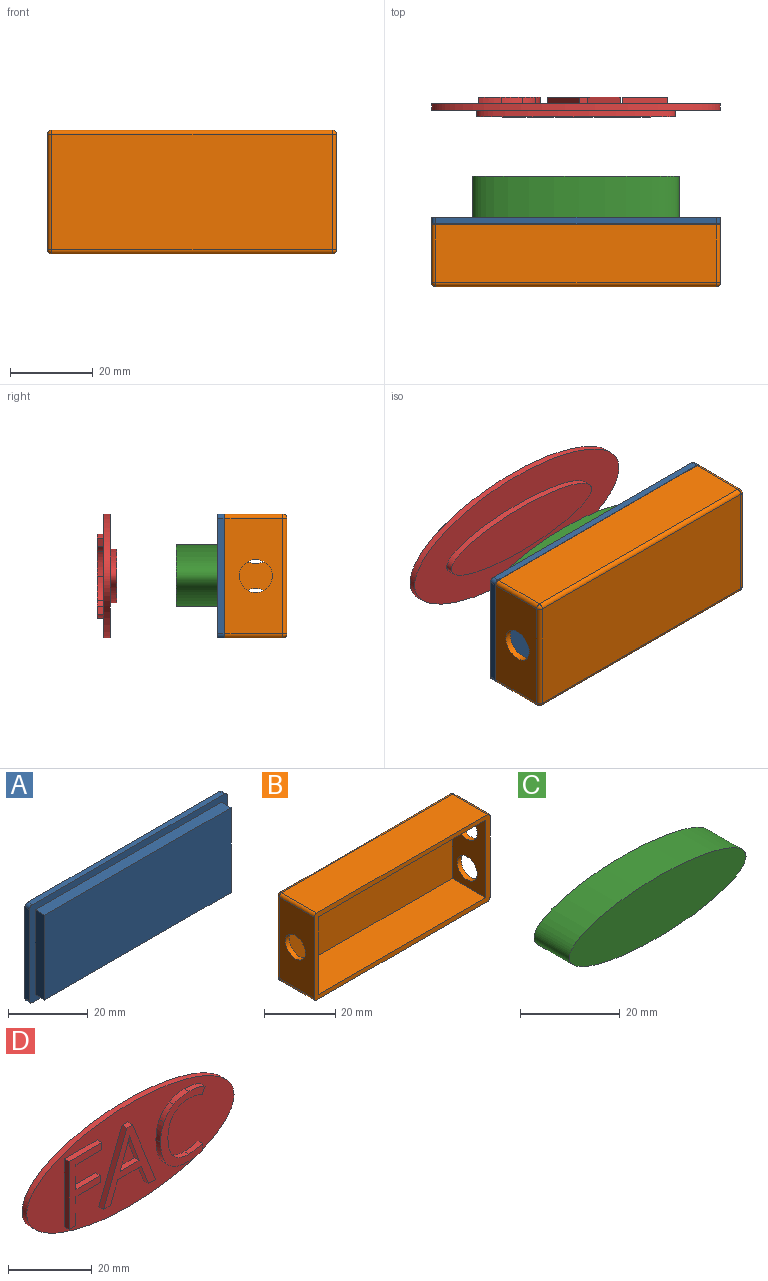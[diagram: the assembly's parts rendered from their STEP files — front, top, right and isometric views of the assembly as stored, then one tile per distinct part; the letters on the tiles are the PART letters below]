
ASSEMBLY  parts=4 mates=2
PART A: 15 faces, bbox 70x5x30 mm
  f0: plane 66x3.4mm, normal (0,0,1), area 224.4mm2, adj f1,f3,f4,f10
  f1: plane 26x3.4mm, normal (-1,0,0), area 88.4mm2, adj f0,f2,f4,f10
  f2: plane 66x3.4mm, normal (0,0,-1), area 224.4mm2, adj f1,f3,f4,f10
  f3: plane 26x3.4mm, normal (1,0,0), area 88.4mm2, adj f0,f2,f4,f10
  f4: plane 66x26mm, normal (0,-1,0), area 1716mm2, adj f0,f1,f2,f3
  f5: plane 70x30mm, normal (0,1,0), area 2099.1mm2, adj f6,f7,f8,f9,f11,f12,f13,f14
  f6: plane 68x1.6mm, normal (0,0,-1), area 108.8mm2, adj f5,f10,f11,f14
  f7: plane 28x1.6mm, normal (1,0,0), area 44.8mm2, adj f5,f10,f13,f14
  f8: plane 68x1.6mm, normal (0,0,1), area 108.8mm2, adj f5,f10,f12,f13
  f9: plane 28x1.6mm, normal (-1,0,0), area 44.8mm2, adj f5,f10,f11,f12
  f10: plane 70x30mm, normal (0,-1,0), area 383.1mm2, adj f0,f1,f2,f3,f6,f7,f8,f9
  f11: cylinder r=1mm len=1.6mm, axis (0,1,0), area 2.5mm2, adj f5,f6,f9,f10
  f12: cylinder r=1mm len=1.6mm, axis (0,-1,0), area 2.5mm2, adj f5,f8,f9,f10
  f13: cylinder r=1mm len=1.6mm, axis (0,1,0), area 2.5mm2, adj f5,f7,f8,f10
  f14: cylinder r=1mm len=1.6mm, axis (0,-1,0), area 2.5mm2, adj f5,f6,f7,f10
PART B: 26 faces, bbox 70x15x30 mm
  f0: plane 68x14mm, normal (0,0,1), area 952mm2, adj f8,f19,f23,f25
  f1: plane 28x14mm, normal (-1,0,0), area 341.7mm2, adj f8,f13,f16,f22,f25
  f2: plane 68x14mm, normal (0,0,-1), area 952mm2, adj f8,f14,f16,f17
  f3: plane 26.8x13.4mm, normal (-1,0,0), area 258.6mm2, adj f4,f6,f8,f10,f11,f12
  f4: plane 66.8x13.4mm, normal (0,0,1), area 895.1mm2, adj f3,f5,f8,f10
  f5: plane 26.8x13.4mm, normal (1,0,0), area 308.9mm2, adj f4,f6,f8,f10,f13
  f6: plane 66.8x13.4mm, normal (0,0,-1), area 895.1mm2, adj f3,f5,f8,f10
  f7: plane 28x14mm, normal (1,0,0), area 291.5mm2, adj f8,f11,f12,f14,f18,f19
  f8: plane 70x30mm, normal (0,-1,0), area 308.9mm2, adj f0,f1,f2,f3,f4,f5,f6,f7
  f9: plane 68x28mm, normal (0,1,0), area 1904mm2, adj f17,f18,f22,f23
  f10: plane 66.8x26.8mm, normal (0,-1,0), area 1790.2mm2, adj f3,f4,f5,f6
  f11: cylinder r=4mm len=8mm, axis (1,0,0), area 40.2mm2, adj f3,f7
  f12: cylinder r=4mm len=8mm, axis (1,0,0), area 40.2mm2, adj f3,f7
  f13: cylinder r=4mm len=8mm, axis (-1,0,0), area 40.2mm2, adj f1,f5
  f14: cylinder r=1mm len=14mm, axis (0,-1,0), area 22mm2, adj f2,f7,f8,f15
  f15: sphere r=1mm, area 1.6mm2, adj f14,f17,f18
  f16: cylinder r=1mm len=14mm, axis (0,1,0), area 22mm2, adj f1,f2,f8,f20
  f17: cylinder r=1mm len=68mm, axis (1,0,0), area 106.8mm2, adj f2,f9,f15,f20
  f18: cylinder r=1mm len=28mm, axis (0,0,1), area 44mm2, adj f7,f9,f15,f21
  f19: cylinder r=1mm len=14mm, axis (0,1,0), area 22mm2, adj f0,f7,f8,f21
  f20: sphere r=1mm, area 1.6mm2, adj f16,f17,f22
  f21: sphere r=1mm, area 1.6mm2, adj f18,f19,f23
  f22: cylinder r=1mm len=28mm, axis (0,0,-1), area 44mm2, adj f1,f9,f20,f24
  f23: cylinder r=1mm len=68mm, axis (-1,0,0), area 106.8mm2, adj f0,f9,f21,f24
  f24: sphere r=1mm, area 1.6mm2, adj f22,f23,f25
  f25: cylinder r=1mm len=14mm, axis (0,-1,0), area 22mm2, adj f0,f1,f8,f24
PART C: 5 faces, bbox 50x10x15 mm
  f0: extruded ~50x15mm, area 1097mm2, adj f1,f2
  f1: plane 50x15mm, normal (0,1,0), area 79.7mm2, adj f0,f3
  f2: plane 50x15mm, normal (0,-1,0), area 589mm2, adj f0
  f3: extruded ~48.4x13.4mm, area 168.1mm2, adj f1,f4
  f4: plane 48.4x13.4mm, normal (0,1,0), area 509.4mm2, adj f3
PART D: 47 faces, bbox 70x4.8x30 mm
  f0: extruded ~70x30mm, area 261.5mm2, adj f1,f35
  f1: plane 70x30mm, normal (0,1,0), area 1159.2mm2, adj f0,f45
  f2: plane 8.48x1.6mm, normal (1,0,0), area 13.6mm2, adj f3,f34,f35,f44
  f3: plane 2.3x1.6mm, normal (0,0,-1), area 3.7mm2, adj f2,f4,f35,f44
  f4: plane 19.83x1.6mm, normal (-1,0,0), area 31.7mm2, adj f3,f5,f35,f44
  f5: plane 11.05x1.6mm, normal (0,0,1), area 17.7mm2, adj f4,f6,f35,f44
  f6: plane 2.05x1.6mm, normal (1,0,0), area 3.3mm2, adj f5,f7,f35,f44
  f7: plane 8.75x1.6mm, normal (0,0,-1), area 14mm2, adj f6,f8,f35,f44
  f8: plane 7.26x1.6mm, normal (1,0,0), area 11.6mm2, adj f7,f9,f35,f44
  f9: plane 8.22x1.6mm, normal (0,0,1), area 13.2mm2, adj f8,f10,f35,f44
  f10: plane 2.05x1.6mm, normal (1,0,0), area 3.3mm2, adj f9,f34,f35,f44
  f11: plane 2.39x1.6mm, normal (0,0,-1), area 3.8mm2, adj f12,f32,f35,f37
  f12: plane 6.31x2.47mm, normal (-0.93,0,-0.36), area 10.8mm2, adj f11,f13,f35,f37
  f13: plane 7.95x1.6mm, normal (0,0,-1), area 12.7mm2, adj f12,f14,f35,f37
  f14: plane 6.31x2.44mm, normal (0.93,0,-0.36), area 10.8mm2, adj f13,f15,f35,f37
  f15: plane 2.34x1.6mm, normal (0,0,-1), area 3.7mm2, adj f14,f16,f35,f37
  f16: plane 19.91x7.84mm, normal (-0.93,0,0.37), area 34.2mm2, adj f15,f17,f35,f37
  f17: plane 1.94x1.6mm, normal (0,0,1), area 3.1mm2, adj f16,f32,f35,f37
  f18: extruded ~4.51x1.6mm, area 7.5mm2, adj f19,f33,f35,f36
  f19: extruded ~5.16x2.18mm, area 9.3mm2, adj f18,f20,f35,f36
  f20: extruded ~5.96x1.89mm, area 10.2mm2, adj f19,f21,f35,f36
  f21: extruded ~6.01x1.83mm, area 10.3mm2, adj f20,f22,f35,f36
  f22: extruded ~5.2x2.12mm, area 9.3mm2, adj f21,f23,f35,f36
  f23: extruded ~4.74x1.6mm, area 7.7mm2, adj f22,f24,f35,f36
  f24: plane 2.02x1.6mm, normal (1,0,0), area 3.2mm2, adj f23,f25,f35,f36
  f25: extruded ~5.09x1.6mm, area 8.3mm2, adj f24,f26,f35,f36
  f26: extruded ~6.76x2.66mm, area 12mm2, adj f25,f27,f35,f36
  f27: extruded ~7.56x2.38mm, area 13mm2, adj f26,f28,f35,f36
  f28: extruded ~5.37x1.6mm, area 8.9mm2, adj f27,f29,f35,f36
  f29: extruded ~3.55x3.31mm, area 7.9mm2, adj f28,f30,f35,f36
  f30: extruded ~5.09x1.6mm, area 8.5mm2, adj f29,f31,f35,f36
  f31: extruded ~5.45x1.6mm, area 9mm2, adj f30,f33,f35,f36
  f32: plane 19.91x7.8mm, normal (0.93,0,0.36), area 34.2mm2, adj f11,f17,f35,f37
  f33: plane 1.98x1.6mm, normal (0.9,0,-0.44), area 3.5mm2, adj f18,f31,f35,f36
  f34: plane 8.22x1.6mm, normal (0,0,-1), area 13.2mm2, adj f2,f10,f35,f44
  f35: plane 70x30mm, normal (0,-1,0), area 1354.1mm2, adj f0,f2,f3,f4,f5,f6,f7,f8
  f36: plane 20.39x15mm, normal (0,-1,0), area 86mm2, adj f18,f19,f20,f21,f22,f23,f24,f25
  f37: plane 19.91x17.58mm, normal (0,-1,0), area 101.2mm2, adj f11,f12,f13,f14,f15,f16,f17,f32
  f38: plane 6.42x1.6mm, normal (0,0,1), area 10.3mm2, adj f37,f39,f42,f43
  f39: plane 6.15x2.31mm, normal (-0.94,0,-0.35), area 10.5mm2, adj f37,f38,f40,f43
  f40: extruded ~2.86x1.6mm, area 4.8mm2, adj f37,f39,f41,f43
  f41: extruded ~2.86x1.6mm, area 4.8mm2, adj f37,f40,f42,f43
  f42: plane 6.15x2.33mm, normal (0.94,0,-0.35), area 10.5mm2, adj f37,f38,f41,f43
  f43: plane 9.01x6.42mm, normal (0,-1,0), area 27.6mm2, adj f38,f39,f40,f41,f42
  f44: plane 19.83x11.05mm, normal (0,-1,0), area 80.5mm2, adj f2,f3,f4,f5,f6,f7,f8,f9
  f45: extruded ~48x13mm, area 166.3mm2, adj f1,f46
  f46: plane 48x13mm, normal (0,1,0), area 490.1mm2, adj f45
PLACE A t=(44.8,4.78,-21.27)mm fixed
PLACE B rot(axis=(1,0,0),180deg) t=(44.8,-12.02,8.73)mm
PLACE C t=(44.8,4.78,-21.2)mm fixed
PLACE D rot(axis=(0,0,1),180deg) t=(9.8,30.73,-6.2)mm
MATE cylindrical D.f46 <-> C.f4  axis (0,-1,0) through (9.8,29.13,-6.2)mm
MATE planar B.f2 <-> A.f8  axis (0,0,1) through (9.8,-4.02,8.73)mm
